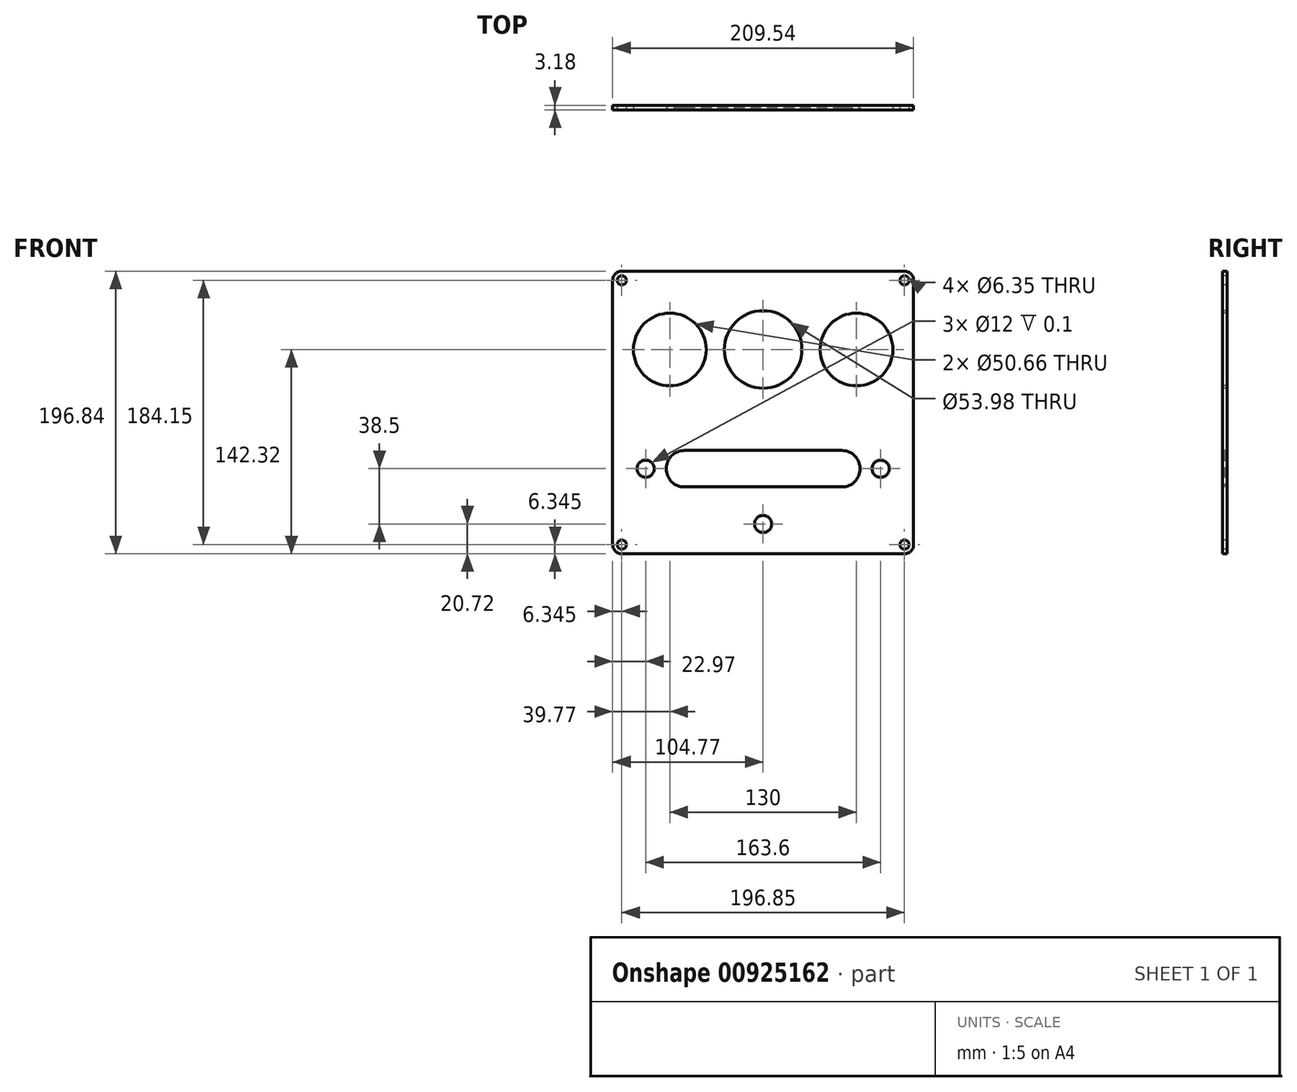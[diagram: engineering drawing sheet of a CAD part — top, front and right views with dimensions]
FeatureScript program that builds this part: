
annotation { "Feature Type Name" : "Feature", "Feature Type Description" : "" }
export const myFeature = defineFeature(function(context is Context, id is Id, definition is map)
    precondition{}
    {
        {
            var Q0;
            Q0=qCreatedBy(makeId("Front.planeOp"),FACE);
            var sketch = newSketch(context, id + "F0", { "sketchPlane" : qUnion([Q0])});
            skLineSegment(sketch, "E0.bottom", {"start": v(-98.43, 98.42) * mm, "end": v(98.43, 98.43) * mm});
            skLineSegment(sketch, "E0.top", {"start": v(-98.43, -98.43) * mm, "end": v(98.43, -98.43) * mm});
            skLineSegment(sketch, "E0.left", {"start": v(-104.78, 92.08) * mm, "end": v(-104.78, -92.08) * mm});
            skLineSegment(sketch, "E0.right", {"start": v(104.78, 92.08) * mm, "end": v(104.78, -92.08) * mm});
            skPoint(sketch, "E1.visualSharp", {"position": v(-104.78, 98.42) * mm});
            skArc(sketch, "E1.filletArc", {"start": v(-98.43, 98.42) * mm, "mid": v(-102.92, 96.57) * mm, "end": v(-104.77, 92.08) * mm});
            skPoint(sketch, "E2.visualSharp", {"position": v(104.78, 98.43) * mm});
            skArc(sketch, "E2.filletArc", {"start": v(104.77, 92.08) * mm, "mid": v(102.92, 96.57) * mm, "end": v(98.43, 98.42) * mm});
            skPoint(sketch, "E3.visualSharp", {"position": v(104.78, -98.43) * mm});
            skArc(sketch, "E3.filletArc", {"start": v(98.43, -98.43) * mm, "mid": v(102.92, -96.57) * mm, "end": v(104.78, -92.08) * mm});
            skPoint(sketch, "E4.visualSharp", {"position": v(-104.78, -98.43) * mm});
            skArc(sketch, "E4.filletArc", {"start": v(-104.78, -92.08) * mm, "mid": v(-102.92, -96.57) * mm, "end": v(-98.43, -98.43) * mm});
            skSolve(sketch);
        }
        {
            var Q0;
            Q0=qSketchRegion(id+"F0",true);
            extrude(context, id + "F1", {"entities" : qUnion([Q0]), "depth" : 3.17 * mm, "offsetDistance" : 25.4 * mm});
        }
        {
            var Q0;
            Q0=makeQuery(id+"F1.opExtrude","CAP_FACE",FACE,{"disambiguationData":[OSD([sQuery(id+"F0.wireOp",EDGE,"E0.bottom"),sQuery(id+"F0.wireOp",EDGE,"E0.top"),sQuery(id+"F0.wireOp",EDGE,"E0.left"),sQuery(id+"F0.wireOp",EDGE,"E0.right"),sQuery(id+"F0.wireOp",EDGE,"E1.filletArc"),sQuery(id+"F0.wireOp",EDGE,"E2.filletArc"),sQuery(id+"F0.wireOp",EDGE,"E3.filletArc"),sQuery(id+"F0.wireOp",EDGE,"E4.filletArc")])],"isStart":false});
            var sketch = newSketch(context, id + "F2", { "sketchPlane" : qUnion([Q0])});
            skCircle(sketch, "E5", {"center": v(-98.43, 92.08) * mm, "radius": 3.18 * mm});
            skCircle(sketch, "E6", {"center": v(98.43, 92.08) * mm, "radius": 3.18 * mm});
            skCircle(sketch, "E7", {"center": v(98.43, -92.08) * mm, "radius": 3.18 * mm});
            skCircle(sketch, "E8", {"center": v(-98.43, -92.08) * mm, "radius": 3.18 * mm});
            skSolve(sketch);
        }
        {
            var Q0;
            Q0=qSketchRegion(id+"F2",true);
            extrude(context, id + "F3", {"entities" : qUnion([Q0]), "operationType" : NewBodyOperationType.REMOVE, "oppositeDirection" : true, "depth" : 25.4 * mm, "offsetDistance" : 25.4 * mm});
        }
        {
            var Q0;
            Q0=makeQuery(id+"F1.opExtrude","CAP_FACE",FACE,{"disambiguationData":[OSD([sQuery(id+"F0.wireOp",EDGE,"E0.bottom"),sQuery(id+"F0.wireOp",EDGE,"E0.top"),sQuery(id+"F0.wireOp",EDGE,"E0.left"),sQuery(id+"F0.wireOp",EDGE,"E0.right"),sQuery(id+"F0.wireOp",EDGE,"E1.filletArc"),sQuery(id+"F0.wireOp",EDGE,"E2.filletArc"),sQuery(id+"F0.wireOp",EDGE,"E3.filletArc"),sQuery(id+"F0.wireOp",EDGE,"E4.filletArc")])],"isStart":false});
            var sketch = newSketch(context, id + "F4", { "sketchPlane" : qUnion([Q0])});
            skLineSegment(sketch, "E9", {"start": v(118.93, 0) * mm, "end": v(-126.64, 0) * mm, "construction": true});
            skLineSegment(sketch, "E10", {"start": v(0, 104.43) * mm, "end": v(0, -104.38) * mm, "construction": true});
            skPoint(sketch, "E10.startSnap0", {"position": v(0, 98.43) * mm});
            skLineSegment(sketch, "E11.bottom", {"start": v(-54.84, -26.5) * mm, "end": v(54.84, -26.5) * mm});
            skLineSegment(sketch, "E11.top", {"start": v(-54.84, -51.9) * mm, "end": v(54.84, -51.9) * mm});
            skLineSegment(sketch, "E11.left", {"start": v(-67.54, -39.2) * mm, "end": v(-67.54, -39.2) * mm});
            skLineSegment(sketch, "E11.right", {"start": v(67.54, -39.2) * mm, "end": v(67.54, -39.2) * mm});
            skPoint(sketch, "E12.visualSharp", {"position": v(-67.54, -26.5) * mm});
            skArc(sketch, "E12.filletArc", {"start": v(-54.84, -26.5) * mm, "mid": v(-63.82, -30.22) * mm, "end": v(-67.54, -39.2) * mm});
            skPoint(sketch, "E13.visualSharp", {"position": v(-67.54, -51.9) * mm});
            skArc(sketch, "E13.filletArc", {"start": v(-67.54, -39.2) * mm, "mid": v(-63.82, -48.18) * mm, "end": v(-54.84, -51.9) * mm});
            skPoint(sketch, "E14.visualSharp", {"position": v(67.54, -26.5) * mm});
            skArc(sketch, "E14.filletArc", {"start": v(67.54, -39.2) * mm, "mid": v(63.82, -30.22) * mm, "end": v(54.84, -26.5) * mm});
            skPoint(sketch, "E15.visualSharp", {"position": v(67.54, -51.9) * mm});
            skArc(sketch, "E15.filletArc", {"start": v(54.84, -51.9) * mm, "mid": v(63.82, -48.18) * mm, "end": v(67.54, -39.2) * mm});
            skSolve(sketch);
        }
        {
            var Q0;
            Q0 = qSketchRegion(id + "F4", true);
            extrude(context, id + "F5", {"entities" : qUnion([Q0]), "operationType" : NewBodyOperationType.REMOVE, "oppositeDirection" : true, "depth" : 1.5 * mm, "offsetDistance" : 25 * mm});
        }
        {
            var Q0;
            Q0=makeQuery(id+"F1.opExtrude","CAP_FACE",FACE,{"disambiguationData":[OSD([sQuery(id+"F0.wireOp",EDGE,"E0.bottom"),sQuery(id+"F0.wireOp",EDGE,"E0.top"),sQuery(id+"F0.wireOp",EDGE,"E0.left"),sQuery(id+"F0.wireOp",EDGE,"E0.right"),sQuery(id+"F0.wireOp",EDGE,"E1.filletArc"),sQuery(id+"F0.wireOp",EDGE,"E2.filletArc"),sQuery(id+"F0.wireOp",EDGE,"E3.filletArc"),sQuery(id+"F0.wireOp",EDGE,"E4.filletArc")])],"isStart":false});
            var sketch = newSketch(context, id + "F6", { "sketchPlane" : qUnion([Q0])});
            skLineSegment(sketch, "E16", {"start": v(0, 0) * mm, "end": v(-63.9, 0) * mm, "construction": true});
            skLineSegment(sketch, "E17", {"start": v(0, 0) * mm, "end": v(0, 44.94) * mm, "construction": true});
            skCircle(sketch, "E18", {"center": v(-81.8, -39.2) * mm, "radius": 6 * mm});
            skCircle(sketch, "E19", {"center": v(0, -77.7) * mm, "radius": 6 * mm});
            skCircle(sketch, "E20.MirrorC", {"center": v(81.8, -39.2) * mm, "radius": 6 * mm});
            skSolve(sketch);
        }
        {
            var Q0;
            Q0 = qSketchRegion(id + "F6", true);
            extrude(context, id + "F7", {"entities" : qUnion([Q0]), "operationType" : NewBodyOperationType.REMOVE, "oppositeDirection" : true, "depth" : 0.1 * mm, "offsetDistance" : 25 * mm});
        }
        {
            var Q0;
            Q0=makeQuery(id+"F1.opExtrude","CAP_FACE",FACE,{"disambiguationData":[OSD([sQuery(id+"F0.wireOp",EDGE,"E0.bottom"),sQuery(id+"F0.wireOp",EDGE,"E0.top"),sQuery(id+"F0.wireOp",EDGE,"E0.left"),sQuery(id+"F0.wireOp",EDGE,"E0.right"),sQuery(id+"F0.wireOp",EDGE,"E1.filletArc"),sQuery(id+"F0.wireOp",EDGE,"E2.filletArc"),sQuery(id+"F0.wireOp",EDGE,"E3.filletArc"),sQuery(id+"F0.wireOp",EDGE,"E4.filletArc")])],"isStart":false});
            var sketch = newSketch(context, id + "F8", { "sketchPlane" : qUnion([Q0])});
            skCircle(sketch, "E21", {"center": v(-65, 43.9) * mm, "radius": 25.33 * mm});
            skLineSegment(sketch, "E22", {"start": v(0, 0) * mm, "end": v(0, 54.45) * mm, "construction": true});
            skPoint(sketch, "E22.endSnap0", {"position": v(0, -26.5) * mm});
            skCircle(sketch, "E23.MirrorC", {"center": v(65, 43.9) * mm, "radius": 25.33 * mm});
            skCircle(sketch, "E24", {"center": v(0, 43.9) * mm, "radius": 26.99 * mm});
            skSolve(sketch);
        }
        {
            var Q0;
            Q0 = qSketchRegion(id + "F8", true);
            extrude(context, id + "F9", {"entities" : qUnion([Q0]), "operationType" : NewBodyOperationType.REMOVE, "endBound" : BoundingType.THROUGH_ALL, "oppositeDirection" : true, "depth" : 25 * mm, "offsetDistance" : 25 * mm});
        }
    });
